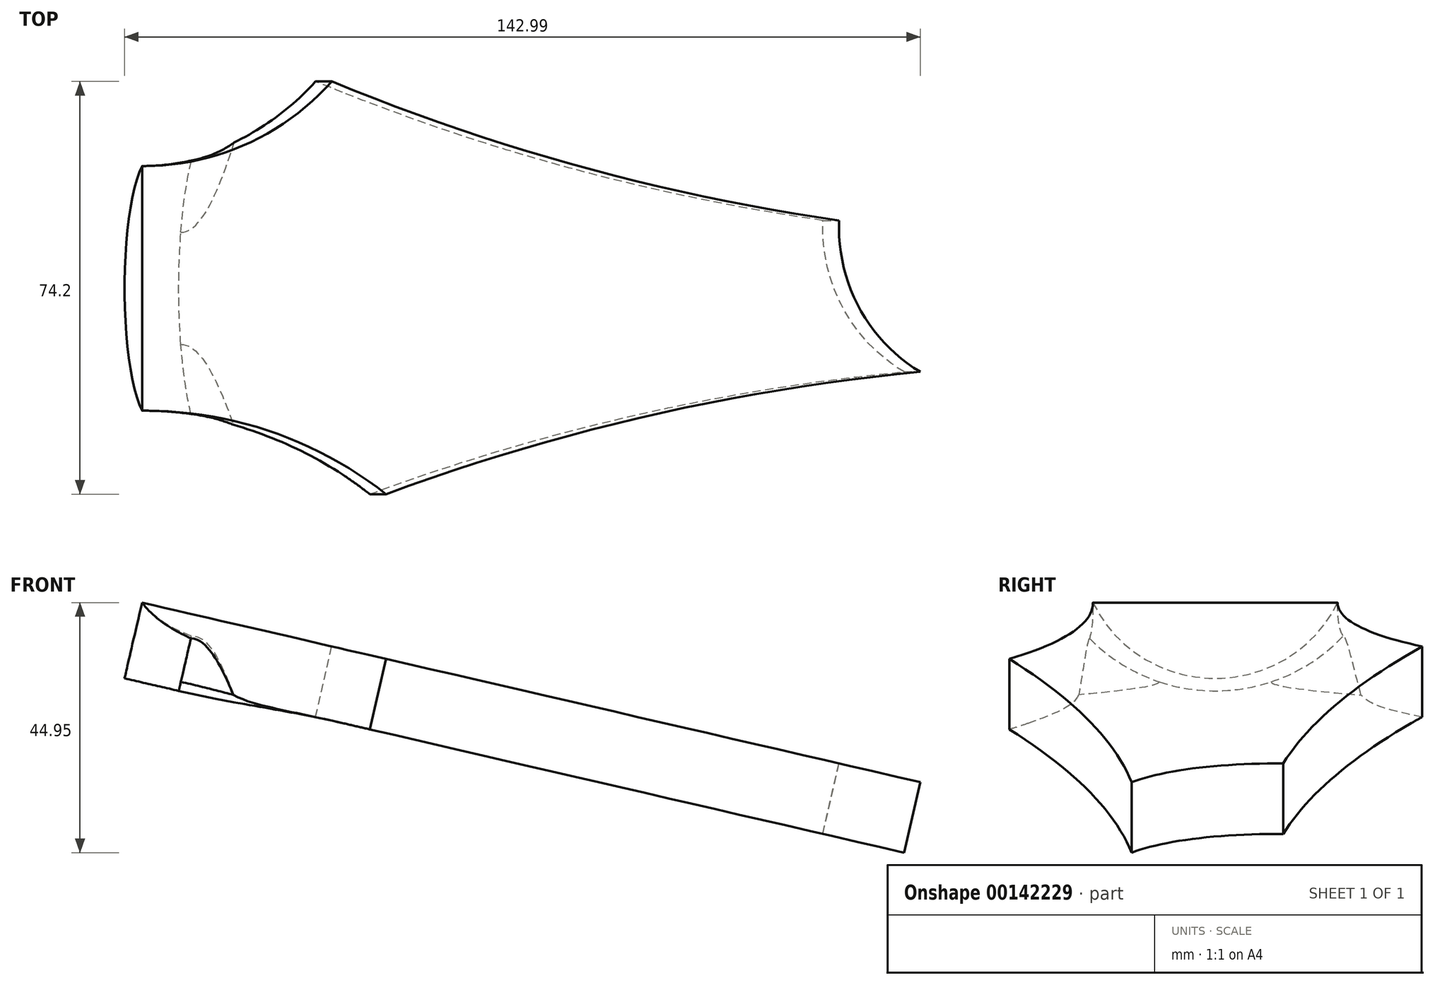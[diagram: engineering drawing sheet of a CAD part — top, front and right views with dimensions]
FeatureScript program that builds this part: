
annotation { "Feature Type Name" : "Feature", "Feature Type Description" : "" }
export const myFeature = defineFeature(function(context is Context, id is Id, definition is map)
    precondition{}
    {
        {
            var Q0;
            Q0=qCreatedBy(makeId("Top.planeOp"),FACE);
            var sketch = newSketch(context, id + "F0", { "sketchPlane" : qUnion([Q0])});
            skLineSegment(sketch, "E0", {"start": v(-562.39, 0) * mm, "end": v(989.83, 0) * mm, "construction": true});
            skLineSegment(sketch, "E1", {"start": v(685.7, 296.13) * mm, "end": v(685.7, -309.82) * mm, "construction": true});
            skLineSegment(sketch, "E2", {"start": v(0, 282.3) * mm, "end": v(0, -300.13) * mm, "construction": true});
            skPoint(sketch, "E3", {"position": v(0, 28.41) * mm});
            skPoint(sketch, "E4.MirrorP", {"position": v(0, -28.41) * mm});
            skPoint(sketch, "E5", {"position": v(685.7, 22) * mm});
            skPoint(sketch, "E6.MirrorP", {"position": v(685.7, -22) * mm});
            skLineSegment(sketch, "E7", {"start": v(0, 28.41) * mm, "end": v(685.7, 22) * mm, "construction": true});
            skLineSegment(sketch, "E8.MirrorCS", {"start": v(0, -28.41) * mm, "end": v(685.7, -22) * mm, "construction": true});
            skLineSegment(sketch, "E9", {"start": v(165.7, 98.55) * mm, "end": v(165.7, -119.87) * mm, "construction": true});
            skLineSegment(sketch, "E10", {"start": v(685.7, -22) * mm, "end": v(165.7, -26.86) * mm});
            skLineSegment(sketch, "E11", {"start": v(165.7, -26.86) * mm, "end": v(165.7, 26.86) * mm});
            skLineSegment(sketch, "E12", {"start": v(165.7, 26.86) * mm, "end": v(685.7, 22) * mm});
            skLineSegment(sketch, "E13", {"start": v(685.7, 22) * mm, "end": v(685.7, -22) * mm});
            skPoint(sketch, "E14.visualSharp", {"position": v(165.7, 26.86) * mm});
            skLineSegment(sketch, "E14.filletArc", {"start": v(165.7, 26.86) * mm, "end": v(165.7, 26.86) * mm});
            skPoint(sketch, "E15.visualSharp", {"position": v(165.7, -26.86) * mm});
            skLineSegment(sketch, "E15.filletArc", {"start": v(165.7, -26.86) * mm, "end": v(165.7, -26.86) * mm});
            skSolve(sketch);
        }
        {
            var Q0;
            Q0 = qSketchRegion(id + "F0", true);
            extrude(context, id + "F1", {"entities" : qUnion([Q0]), "depth" : 6 * mm});
        }
        {
            var Q0;
            Q0=makeQuery(id+"F1.opExtrude","SWEPT_FACE",FACE,{"disambiguationData":[OSD([sQuery(id+"F0.wireOp",EDGE,"E11")])]});
            var sketch = newSketch(context, id + "F2", { "sketchPlane" : qUnion([Q0])});
            skPoint(sketch, "E16", {"position": v(0, 6) * mm});
            skCircle(sketch, "E17", {"center": v(0, -400.4) * mm, "radius": 406.4 * mm});
            skSolve(sketch);
        }
        {
            var Q0;
            Q0 = qSketchRegion(id + "F2", true);
            extrude(context, id + "F3", {"entities" : qUnion([Q0]), "oppositeDirection" : true, "depth" : 520 * mm});
        }
        {
            var Q0;
            Q0=makeQuery(id+"F1.opExtrude","SWEPT_BODY",BODY,{"disambiguationData":[OSD([sQuery(id+"F0.wireOp",EDGE,"E10"),sQuery(id+"F0.wireOp",EDGE,"E11"),sQuery(id+"F0.wireOp",EDGE,"E12"),sQuery(id+"F0.wireOp",EDGE,"E13")])]});
            var Q1;
            Q1=makeQuery(id+"F3.opExtrude","SWEPT_BODY",BODY,{"disambiguationData":[OSD([sQuery(id+"F2.wireOp",EDGE,"E17")])]});
            booleanBodies(context, id + "F4", {"operationType" : BooleanOperationType.INTERSECTION, "tools" : qUnion([Q0, Q1])});
        }
        {
            var Q0;
            Q0=qCreatedBy(makeId("Top.planeOp"),FACE);
            var sketch = newSketch(context, id + "F5", { "sketchPlane" : qUnion([Q0])});
            skLineSegment(sketch, "E18.0", {"start": v(685.7, 296.13) * mm, "end": v(685.7, -309.82) * mm, "construction": true});
            skLineSegment(sketch, "E18.1", {"start": v(165.7, 98.55) * mm, "end": v(165.7, -119.87) * mm, "construction": true});
            skLineSegment(sketch, "E19.0", {"start": v(685.7, -22) * mm, "end": v(165.7, -26.86) * mm, "construction": true});
            skLineSegment(sketch, "E19.2", {"start": v(165.7, 26.86) * mm, "end": v(685.7, 22) * mm, "construction": true});
            skPoint(sketch, "E20", {"position": v(204.04, 0) * mm});
            skPoint(sketch, "E21", {"position": v(647.25, 0) * mm});
            skPoint(sketch, "E22", {"position": v(610.95, 0) * mm});
            skPoint(sketch, "E23", {"position": v(576.7, 0) * mm});
            skPoint(sketch, "E24", {"position": v(544.35, 0) * mm});
            skPoint(sketch, "E25", {"position": v(513.82, 0) * mm});
            skPoint(sketch, "E26", {"position": v(485, 0) * mm});
            skPoint(sketch, "E27", {"position": v(457.8, 0) * mm});
            skPoint(sketch, "E28", {"position": v(432.13, 0) * mm});
            skPoint(sketch, "E29", {"position": v(407.9, 0) * mm});
            skPoint(sketch, "E30", {"position": v(385.02, 0) * mm});
            skPoint(sketch, "E31", {"position": v(363.43, 0) * mm});
            skPoint(sketch, "E32", {"position": v(343.05, 0) * mm});
            skPoint(sketch, "E33", {"position": v(323.8, 0) * mm});
            skPoint(sketch, "E34", {"position": v(305.64, 0) * mm});
            skPoint(sketch, "E35", {"position": v(288.5, 0) * mm});
            skPoint(sketch, "E36", {"position": v(272.32, 0) * mm});
            skPoint(sketch, "E37", {"position": v(257.05, 0) * mm});
            skPoint(sketch, "E38", {"position": v(242.63, 0) * mm});
            skPoint(sketch, "E39", {"position": v(229.02, 0) * mm});
            skPoint(sketch, "E40", {"position": v(216.17, 0) * mm});
            skPoint(sketch, "E41", {"position": v(192.6, 0) * mm});
            skPoint(sketch, "E42", {"position": v(181.8, 0) * mm});
            skPoint(sketch, "E43", {"position": v(171.6, 0) * mm});
            skLineSegment(sketch, "E44", {"start": v(648.39, 22.35) * mm, "end": v(648.39, -22.35) * mm});
            skLineSegment(sketch, "E45", {"start": v(646.1, 22.37) * mm, "end": v(646.1, -22.37) * mm});
            skLineSegment(sketch, "E46", {"start": v(646.1, 22.37) * mm, "end": v(648.39, 22.35) * mm});
            skLineSegment(sketch, "E47", {"start": v(646.1, -22.37) * mm, "end": v(648.39, -22.35) * mm});
            skLineSegment(sketch, "E48", {"start": v(612.1, -22.69) * mm, "end": v(612.1, 22.69) * mm});
            skLineSegment(sketch, "E49", {"start": v(609.81, -22.7) * mm, "end": v(609.81, 22.7) * mm});
            skLineSegment(sketch, "E50", {"start": v(577.83, -23) * mm, "end": v(577.83, 23) * mm});
            skLineSegment(sketch, "E51", {"start": v(575.55, -23.03) * mm, "end": v(575.55, 23.03) * mm});
            skLineSegment(sketch, "E52", {"start": v(545.49, -23.31) * mm, "end": v(545.49, 23.31) * mm});
            skLineSegment(sketch, "E53", {"start": v(609.81, -22.7) * mm, "end": v(612.1, -22.69) * mm});
            skLineSegment(sketch, "E54", {"start": v(609.81, 22.7) * mm, "end": v(612.1, 22.69) * mm});
            skLineSegment(sketch, "E55", {"start": v(575.55, 23.03) * mm, "end": v(577.83, 23) * mm});
            skLineSegment(sketch, "E56", {"start": v(575.55, -23.03) * mm, "end": v(577.83, -23) * mm});
            skLineSegment(sketch, "E57", {"start": v(543.2, 23.33) * mm, "end": v(543.2, -23.33) * mm});
            skLineSegment(sketch, "E58", {"start": v(514.96, 23.6) * mm, "end": v(514.96, -23.6) * mm});
            skLineSegment(sketch, "E59", {"start": v(512.68, 23.62) * mm, "end": v(512.68, -23.62) * mm});
            skLineSegment(sketch, "E60", {"start": v(486.15, 23.87) * mm, "end": v(486.15, -23.87) * mm});
            skLineSegment(sketch, "E61", {"start": v(483.87, 23.89) * mm, "end": v(483.87, -23.89) * mm});
            skLineSegment(sketch, "E62", {"start": v(458.95, 24.12) * mm, "end": v(458.95, -24.12) * mm});
            skLineSegment(sketch, "E63", {"start": v(456.67, 24.14) * mm, "end": v(456.67, -24.14) * mm});
            skLineSegment(sketch, "E64", {"start": v(433.27, -24.36) * mm, "end": v(433.27, 24.36) * mm});
            skLineSegment(sketch, "E65", {"start": v(431, -24.38) * mm, "end": v(431, 24.38) * mm});
            skLineSegment(sketch, "E66", {"start": v(409.04, -24.59) * mm, "end": v(409.04, 24.59) * mm});
            skLineSegment(sketch, "E67", {"start": v(406.76, -24.6) * mm, "end": v(406.76, 24.6) * mm});
            skLineSegment(sketch, "E68", {"start": v(543.2, -23.33) * mm, "end": v(545.49, -23.31) * mm});
            skLineSegment(sketch, "E69", {"start": v(512.68, -23.62) * mm, "end": v(514.96, -23.6) * mm});
            skLineSegment(sketch, "E70", {"start": v(483.87, -23.89) * mm, "end": v(486.15, -23.87) * mm});
            skLineSegment(sketch, "E71", {"start": v(456.67, -24.14) * mm, "end": v(458.95, -24.12) * mm});
            skLineSegment(sketch, "E72", {"start": v(431, -24.38) * mm, "end": v(433.27, -24.36) * mm});
            skLineSegment(sketch, "E73", {"start": v(431, 24.38) * mm, "end": v(433.27, 24.36) * mm});
            skLineSegment(sketch, "E74", {"start": v(456.67, 24.14) * mm, "end": v(458.95, 24.12) * mm});
            skLineSegment(sketch, "E75", {"start": v(483.87, 23.89) * mm, "end": v(486.15, 23.87) * mm});
            skLineSegment(sketch, "E76", {"start": v(512.68, 23.62) * mm, "end": v(514.96, 23.6) * mm});
            skLineSegment(sketch, "E77", {"start": v(543.2, 23.33) * mm, "end": v(545.49, 23.31) * mm});
            skLineSegment(sketch, "E78", {"start": v(386.16, 24.8) * mm, "end": v(386.16, -24.8) * mm});
            skLineSegment(sketch, "E79", {"start": v(383.88, 24.82) * mm, "end": v(383.88, -24.82) * mm});
            skLineSegment(sketch, "E80", {"start": v(364.57, 25) * mm, "end": v(364.57, -25) * mm});
            skLineSegment(sketch, "E81", {"start": v(362.52, 25.02) * mm, "end": v(362.05, -25.03) * mm});
            skLineSegment(sketch, "E82", {"start": v(409.04, -24.59) * mm, "end": v(406.76, -24.6) * mm});
            skLineSegment(sketch, "E83", {"start": v(406.76, 24.6) * mm, "end": v(409.04, 24.59) * mm});
            skLineSegment(sketch, "E84", {"start": v(383.88, 24.82) * mm, "end": v(386.16, 24.8) * mm});
            skLineSegment(sketch, "E85", {"start": v(383.88, -24.82) * mm, "end": v(386.16, -24.8) * mm});
            skLineSegment(sketch, "E86", {"start": v(364.57, -25) * mm, "end": v(362.05, -25.03) * mm});
            skLineSegment(sketch, "E87", {"start": v(362.52, 25.02) * mm, "end": v(364.57, 25) * mm});
            skLineSegment(sketch, "E88", {"start": v(344.19, 25.2) * mm, "end": v(344.19, -25.2) * mm});
            skLineSegment(sketch, "E89", {"start": v(341.9, -25.22) * mm, "end": v(341.9, 25.22) * mm});
            skLineSegment(sketch, "E90", {"start": v(324.95, -25.38) * mm, "end": v(324.95, 25.38) * mm});
            skLineSegment(sketch, "E91", {"start": v(322.67, -25.4) * mm, "end": v(322.67, 25.4) * mm});
            skLineSegment(sketch, "E92", {"start": v(306.78, -25.54) * mm, "end": v(306.78, 25.54) * mm});
            skLineSegment(sketch, "E93", {"start": v(304.5, -25.57) * mm, "end": v(304.5, 25.57) * mm});
            skLineSegment(sketch, "E94", {"start": v(289.64, -25.7) * mm, "end": v(289.64, 25.7) * mm});
            skLineSegment(sketch, "E95", {"start": v(287.36, -25.73) * mm, "end": v(287.36, 25.73) * mm});
            skLineSegment(sketch, "E96", {"start": v(273.46, -25.86) * mm, "end": v(273.46, 25.86) * mm});
            skLineSegment(sketch, "E97", {"start": v(271.18, -25.88) * mm, "end": v(271.18, 25.88) * mm});
            skLineSegment(sketch, "E98", {"start": v(344.19, -25.2) * mm, "end": v(341.9, -25.22) * mm});
            skLineSegment(sketch, "E99", {"start": v(324.95, -25.38) * mm, "end": v(322.67, -25.4) * mm});
            skLineSegment(sketch, "E100", {"start": v(289.64, -25.7) * mm, "end": v(287.36, -25.73) * mm});
            skLineSegment(sketch, "E101", {"start": v(273.46, -25.86) * mm, "end": v(271.18, -25.88) * mm});
            skLineSegment(sketch, "E102", {"start": v(271.18, 25.88) * mm, "end": v(273.46, 25.86) * mm});
            skLineSegment(sketch, "E103", {"start": v(287.36, 25.73) * mm, "end": v(289.64, 25.7) * mm});
            skLineSegment(sketch, "E104", {"start": v(304.5, 25.57) * mm, "end": v(306.78, 25.54) * mm});
            skLineSegment(sketch, "E105", {"start": v(322.67, 25.4) * mm, "end": v(324.95, 25.38) * mm});
            skLineSegment(sketch, "E106", {"start": v(304.5, -25.57) * mm, "end": v(306.78, -25.54) * mm});
            skLineSegment(sketch, "E107", {"start": v(341.9, 25.22) * mm, "end": v(344.19, 25.2) * mm});
            skLineSegment(sketch, "E108", {"start": v(258.19, -26) * mm, "end": v(258.19, 26) * mm});
            skLineSegment(sketch, "E109", {"start": v(243.77, -26.13) * mm, "end": v(243.77, 26.13) * mm});
            skLineSegment(sketch, "E110", {"start": v(230.16, -26.26) * mm, "end": v(230.16, 26.26) * mm});
            skLineSegment(sketch, "E111", {"start": v(217.31, -26.38) * mm, "end": v(217.31, 26.38) * mm});
            skLineSegment(sketch, "E112", {"start": v(205.18, -26.5) * mm, "end": v(205.18, 26.5) * mm});
            skLineSegment(sketch, "E113", {"start": v(193.74, -26.6) * mm, "end": v(193.74, 26.6) * mm});
            skLineSegment(sketch, "E114", {"start": v(182.93, -26.7) * mm, "end": v(182.93, 26.7) * mm});
            skLineSegment(sketch, "E115", {"start": v(172.74, -26.8) * mm, "end": v(172.74, 26.8) * mm});
            skLineSegment(sketch, "E116", {"start": v(170.46, -26.82) * mm, "end": v(170.46, 26.8) * mm});
            skLineSegment(sketch, "E117", {"start": v(180.65, -26.72) * mm, "end": v(180.65, 26.72) * mm});
            skLineSegment(sketch, "E118", {"start": v(191.46, -26.62) * mm, "end": v(191.46, 26.62) * mm});
            skLineSegment(sketch, "E119", {"start": v(202.9, -26.52) * mm, "end": v(202.9, 26.52) * mm});
            skLineSegment(sketch, "E120", {"start": v(215.03, -26.4) * mm, "end": v(215.03, 26.4) * mm});
            skLineSegment(sketch, "E121", {"start": v(227.88, -26.28) * mm, "end": v(227.88, 26.28) * mm});
            skLineSegment(sketch, "E122", {"start": v(241.49, -26.16) * mm, "end": v(241.49, 26.16) * mm});
            skLineSegment(sketch, "E123", {"start": v(255.9, -26.02) * mm, "end": v(255.9, 26.02) * mm});
            skLineSegment(sketch, "E124", {"start": v(258.19, -26) * mm, "end": v(255.9, -26.02) * mm});
            skLineSegment(sketch, "E125", {"start": v(243.77, -26.13) * mm, "end": v(241.49, -26.16) * mm});
            skLineSegment(sketch, "E126", {"start": v(230.16, -26.26) * mm, "end": v(227.88, -26.28) * mm});
            skLineSegment(sketch, "E127", {"start": v(217.31, -26.38) * mm, "end": v(215.03, -26.4) * mm});
            skLineSegment(sketch, "E128", {"start": v(205.18, -26.5) * mm, "end": v(202.9, -26.52) * mm});
            skLineSegment(sketch, "E129", {"start": v(193.74, -26.6) * mm, "end": v(191.46, -26.62) * mm});
            skLineSegment(sketch, "E130", {"start": v(182.93, -26.7) * mm, "end": v(180.65, -26.72) * mm});
            skLineSegment(sketch, "E131", {"start": v(172.74, -26.8) * mm, "end": v(170.46, -26.82) * mm});
            skLineSegment(sketch, "E132", {"start": v(170.46, 26.8) * mm, "end": v(172.74, 26.8) * mm});
            skLineSegment(sketch, "E133", {"start": v(180.65, 26.72) * mm, "end": v(182.93, 26.7) * mm});
            skLineSegment(sketch, "E134", {"start": v(191.46, 26.62) * mm, "end": v(193.74, 26.6) * mm});
            skLineSegment(sketch, "E135", {"start": v(202.9, 26.52) * mm, "end": v(205.18, 26.5) * mm});
            skLineSegment(sketch, "E136", {"start": v(215.03, 26.4) * mm, "end": v(217.31, 26.38) * mm});
            skLineSegment(sketch, "E137", {"start": v(227.88, 26.28) * mm, "end": v(230.16, 26.26) * mm});
            skLineSegment(sketch, "E138", {"start": v(241.49, 26.16) * mm, "end": v(243.77, 26.13) * mm});
            skLineSegment(sketch, "E139", {"start": v(255.9, 26.02) * mm, "end": v(258.19, 26) * mm});
            skSolve(sketch);
        }
        {
            var Q0;
            Q0 = qSketchRegion(id + "F5", true);
            extrude(context, id + "F6", {"entities" : qUnion([Q0]), "operationType" : NewBodyOperationType.ADD, "depth" : 7.4 * mm});
        }
        {
            var Q0;
            Q0=makeQuery(id+"F1.opExtrude","SWEPT_FACE",FACE,{"disambiguationData":[OSD([sQuery(id+"F0.wireOp",EDGE,"E11")])]});
            var sketch = newSketch(context, id + "F7", { "sketchPlane" : qUnion([Q0])});
            skCircle(sketch, "E140.0", {"center": v(0, -400.4) * mm, "radius": 406.4 * mm, "construction": true});
            skCircle(sketch, "E141", {"center": v(0, -399) * mm, "radius": 406.4 * mm});
            skSolve(sketch);
        }
        {
            var Q0;
            Q0 = qSketchRegion(id + "F7", true);
            extrude(context, id + "F8", {"entities" : qUnion([Q0]), "oppositeDirection" : true, "depth" : 520 * mm});
        }
        {
            var Q0;
            Q0=makeQuery(id+"F4.opBoolean","INTERSECT",BODY,{"derivedFrom":[makeQuery(id+"F1.opExtrude","SWEPT_BODY",BODY,{"disambiguationData":[OSD([sQuery(id+"F0.wireOp",EDGE,"E10"),sQuery(id+"F0.wireOp",EDGE,"E11"),sQuery(id+"F0.wireOp",EDGE,"E12"),sQuery(id+"F0.wireOp",EDGE,"E13")])]}),makeQuery(id+"F3.opExtrude","SWEPT_BODY",BODY,{"disambiguationData":[OSD([sQuery(id+"F2.wireOp",EDGE,"E17")])]})]});
            var Q1;
            Q1=makeQuery(id+"F8.opExtrude","SWEPT_BODY",BODY,{"disambiguationData":[OSD([sQuery(id+"F7.wireOp",EDGE,"E141")])]});
            booleanBodies(context, id + "F9", {"operationType" : BooleanOperationType.INTERSECTION, "tools" : qUnion([Q0, Q1])});
        }
        {
            var Q0;
            Q0=makeQuery(id+"F9.opBoolean","INTERSECT",EDGE,{"derivedFrom":[makeQuery(id+"F6.opExtrude","SWEPT_FACE",FACE,{"disambiguationData":[OSD([sQuery(id+"F5.wireOp",EDGE,"E116")])]}),makeQuery(id+"F8.opExtrude","SWEPT_FACE",FACE,{"disambiguationData":[OSD([sQuery(id+"F7.wireOp",EDGE,"E141")])]})]});
            var Q1;
            Q1=makeQuery(id+"F9.opBoolean","INTERSECT",EDGE,{"derivedFrom":[makeQuery(id+"F6.opExtrude","SWEPT_FACE",FACE,{"disambiguationData":[OSD([sQuery(id+"F5.wireOp",EDGE,"E115")])]}),makeQuery(id+"F8.opExtrude","SWEPT_FACE",FACE,{"disambiguationData":[OSD([sQuery(id+"F7.wireOp",EDGE,"E141")])]})]});
            var Q2;
            Q2=makeQuery(id+"F9.opBoolean","INTERSECT",EDGE,{"derivedFrom":[makeQuery(id+"F6.opExtrude","SWEPT_FACE",FACE,{"disambiguationData":[OSD([sQuery(id+"F5.wireOp",EDGE,"E117")])]}),makeQuery(id+"F8.opExtrude","SWEPT_FACE",FACE,{"disambiguationData":[OSD([sQuery(id+"F7.wireOp",EDGE,"E141")])]})]});
            var Q3;
            Q3=makeQuery(id+"F9.opBoolean","INTERSECT",EDGE,{"derivedFrom":[makeQuery(id+"F6.opExtrude","SWEPT_FACE",FACE,{"disambiguationData":[OSD([sQuery(id+"F5.wireOp",EDGE,"E114")])]}),makeQuery(id+"F8.opExtrude","SWEPT_FACE",FACE,{"disambiguationData":[OSD([sQuery(id+"F7.wireOp",EDGE,"E141")])]})]});
            var Q4;
            Q4=makeQuery(id+"F9.opBoolean","INTERSECT",EDGE,{"derivedFrom":[makeQuery(id+"F6.opExtrude","SWEPT_FACE",FACE,{"disambiguationData":[OSD([sQuery(id+"F5.wireOp",EDGE,"E118")])]}),makeQuery(id+"F8.opExtrude","SWEPT_FACE",FACE,{"disambiguationData":[OSD([sQuery(id+"F7.wireOp",EDGE,"E141")])]})]});
            var Q5;
            Q5=makeQuery(id+"F9.opBoolean","INTERSECT",EDGE,{"derivedFrom":[makeQuery(id+"F6.opExtrude","SWEPT_FACE",FACE,{"disambiguationData":[OSD([sQuery(id+"F5.wireOp",EDGE,"E113")])]}),makeQuery(id+"F8.opExtrude","SWEPT_FACE",FACE,{"disambiguationData":[OSD([sQuery(id+"F7.wireOp",EDGE,"E141")])]})]});
            var Q6;
            Q6=makeQuery(id+"F9.opBoolean","INTERSECT",EDGE,{"derivedFrom":[makeQuery(id+"F6.opExtrude","SWEPT_FACE",FACE,{"disambiguationData":[OSD([sQuery(id+"F5.wireOp",EDGE,"E119")])]}),makeQuery(id+"F8.opExtrude","SWEPT_FACE",FACE,{"disambiguationData":[OSD([sQuery(id+"F7.wireOp",EDGE,"E141")])]})]});
            var Q7;
            Q7=makeQuery(id+"F9.opBoolean","INTERSECT",EDGE,{"derivedFrom":[makeQuery(id+"F6.opExtrude","SWEPT_FACE",FACE,{"disambiguationData":[OSD([sQuery(id+"F5.wireOp",EDGE,"E112")])]}),makeQuery(id+"F8.opExtrude","SWEPT_FACE",FACE,{"disambiguationData":[OSD([sQuery(id+"F7.wireOp",EDGE,"E141")])]})]});
            var Q8;
            Q8=makeQuery(id+"F9.opBoolean","INTERSECT",EDGE,{"derivedFrom":[makeQuery(id+"F6.opExtrude","SWEPT_FACE",FACE,{"disambiguationData":[OSD([sQuery(id+"F5.wireOp",EDGE,"E120")])]}),makeQuery(id+"F8.opExtrude","SWEPT_FACE",FACE,{"disambiguationData":[OSD([sQuery(id+"F7.wireOp",EDGE,"E141")])]})]});
            var Q9;
            Q9=makeQuery(id+"F9.opBoolean","INTERSECT",EDGE,{"derivedFrom":[makeQuery(id+"F6.opExtrude","SWEPT_FACE",FACE,{"disambiguationData":[OSD([sQuery(id+"F5.wireOp",EDGE,"E111")])]}),makeQuery(id+"F8.opExtrude","SWEPT_FACE",FACE,{"disambiguationData":[OSD([sQuery(id+"F7.wireOp",EDGE,"E141")])]})]});
            var Q10;
            Q10=makeQuery(id+"F9.opBoolean","INTERSECT",EDGE,{"derivedFrom":[makeQuery(id+"F6.opExtrude","SWEPT_FACE",FACE,{"disambiguationData":[OSD([sQuery(id+"F5.wireOp",EDGE,"E121")])]}),makeQuery(id+"F8.opExtrude","SWEPT_FACE",FACE,{"disambiguationData":[OSD([sQuery(id+"F7.wireOp",EDGE,"E141")])]})]});
            var Q11;
            Q11=makeQuery(id+"F9.opBoolean","INTERSECT",EDGE,{"derivedFrom":[makeQuery(id+"F6.opExtrude","SWEPT_FACE",FACE,{"disambiguationData":[OSD([sQuery(id+"F5.wireOp",EDGE,"E110")])]}),makeQuery(id+"F8.opExtrude","SWEPT_FACE",FACE,{"disambiguationData":[OSD([sQuery(id+"F7.wireOp",EDGE,"E141")])]})]});
            var Q12;
            Q12=makeQuery(id+"F9.opBoolean","INTERSECT",EDGE,{"derivedFrom":[makeQuery(id+"F6.opExtrude","SWEPT_FACE",FACE,{"disambiguationData":[OSD([sQuery(id+"F5.wireOp",EDGE,"E122")])]}),makeQuery(id+"F8.opExtrude","SWEPT_FACE",FACE,{"disambiguationData":[OSD([sQuery(id+"F7.wireOp",EDGE,"E141")])]})]});
            var Q13;
            Q13=makeQuery(id+"F9.opBoolean","INTERSECT",EDGE,{"derivedFrom":[makeQuery(id+"F6.opExtrude","SWEPT_FACE",FACE,{"disambiguationData":[OSD([sQuery(id+"F5.wireOp",EDGE,"E109")])]}),makeQuery(id+"F8.opExtrude","SWEPT_FACE",FACE,{"disambiguationData":[OSD([sQuery(id+"F7.wireOp",EDGE,"E141")])]})]});
            var Q14;
            Q14=makeQuery(id+"F9.opBoolean","INTERSECT",EDGE,{"derivedFrom":[makeQuery(id+"F6.opExtrude","SWEPT_FACE",FACE,{"disambiguationData":[OSD([sQuery(id+"F5.wireOp",EDGE,"E123")])]}),makeQuery(id+"F8.opExtrude","SWEPT_FACE",FACE,{"disambiguationData":[OSD([sQuery(id+"F7.wireOp",EDGE,"E141")])]})]});
            var Q15;
            Q15=makeQuery(id+"F9.opBoolean","INTERSECT",EDGE,{"derivedFrom":[makeQuery(id+"F6.opExtrude","SWEPT_FACE",FACE,{"disambiguationData":[OSD([sQuery(id+"F5.wireOp",EDGE,"E108")])]}),makeQuery(id+"F8.opExtrude","SWEPT_FACE",FACE,{"disambiguationData":[OSD([sQuery(id+"F7.wireOp",EDGE,"E141")])]})]});
            var Q16;
            Q16=makeQuery(id+"F9.opBoolean","INTERSECT",EDGE,{"derivedFrom":[makeQuery(id+"F6.opExtrude","SWEPT_FACE",FACE,{"disambiguationData":[OSD([sQuery(id+"F5.wireOp",EDGE,"E97")])]}),makeQuery(id+"F8.opExtrude","SWEPT_FACE",FACE,{"disambiguationData":[OSD([sQuery(id+"F7.wireOp",EDGE,"E141")])]})]});
            var Q17;
            Q17=makeQuery(id+"F9.opBoolean","INTERSECT",EDGE,{"derivedFrom":[makeQuery(id+"F6.opExtrude","SWEPT_FACE",FACE,{"disambiguationData":[OSD([sQuery(id+"F5.wireOp",EDGE,"E96")])]}),makeQuery(id+"F8.opExtrude","SWEPT_FACE",FACE,{"disambiguationData":[OSD([sQuery(id+"F7.wireOp",EDGE,"E141")])]})]});
            var Q18;
            Q18=makeQuery(id+"F9.opBoolean","INTERSECT",EDGE,{"derivedFrom":[makeQuery(id+"F6.opExtrude","SWEPT_FACE",FACE,{"disambiguationData":[OSD([sQuery(id+"F5.wireOp",EDGE,"E95")])]}),makeQuery(id+"F8.opExtrude","SWEPT_FACE",FACE,{"disambiguationData":[OSD([sQuery(id+"F7.wireOp",EDGE,"E141")])]})]});
            var Q19;
            Q19=makeQuery(id+"F9.opBoolean","INTERSECT",EDGE,{"derivedFrom":[makeQuery(id+"F6.opExtrude","SWEPT_FACE",FACE,{"disambiguationData":[OSD([sQuery(id+"F5.wireOp",EDGE,"E94")])]}),makeQuery(id+"F8.opExtrude","SWEPT_FACE",FACE,{"disambiguationData":[OSD([sQuery(id+"F7.wireOp",EDGE,"E141")])]})]});
            var Q20;
            Q20=makeQuery(id+"F9.opBoolean","INTERSECT",EDGE,{"derivedFrom":[makeQuery(id+"F6.opExtrude","SWEPT_FACE",FACE,{"disambiguationData":[OSD([sQuery(id+"F5.wireOp",EDGE,"E93")])]}),makeQuery(id+"F8.opExtrude","SWEPT_FACE",FACE,{"disambiguationData":[OSD([sQuery(id+"F7.wireOp",EDGE,"E141")])]})]});
            var Q21;
            Q21=makeQuery(id+"F9.opBoolean","INTERSECT",EDGE,{"derivedFrom":[makeQuery(id+"F6.opExtrude","SWEPT_FACE",FACE,{"disambiguationData":[OSD([sQuery(id+"F5.wireOp",EDGE,"E92")])]}),makeQuery(id+"F8.opExtrude","SWEPT_FACE",FACE,{"disambiguationData":[OSD([sQuery(id+"F7.wireOp",EDGE,"E141")])]})]});
            var Q22;
            Q22=makeQuery(id+"F9.opBoolean","INTERSECT",EDGE,{"derivedFrom":[makeQuery(id+"F6.opExtrude","SWEPT_FACE",FACE,{"disambiguationData":[OSD([sQuery(id+"F5.wireOp",EDGE,"E91")])]}),makeQuery(id+"F8.opExtrude","SWEPT_FACE",FACE,{"disambiguationData":[OSD([sQuery(id+"F7.wireOp",EDGE,"E141")])]})]});
            var Q23;
            Q23=makeQuery(id+"F9.opBoolean","INTERSECT",EDGE,{"derivedFrom":[makeQuery(id+"F6.opExtrude","SWEPT_FACE",FACE,{"disambiguationData":[OSD([sQuery(id+"F5.wireOp",EDGE,"E90")])]}),makeQuery(id+"F8.opExtrude","SWEPT_FACE",FACE,{"disambiguationData":[OSD([sQuery(id+"F7.wireOp",EDGE,"E141")])]})]});
            var Q24;
            Q24=makeQuery(id+"F9.opBoolean","INTERSECT",EDGE,{"derivedFrom":[makeQuery(id+"F6.opExtrude","SWEPT_FACE",FACE,{"disambiguationData":[OSD([sQuery(id+"F5.wireOp",EDGE,"E89")])]}),makeQuery(id+"F8.opExtrude","SWEPT_FACE",FACE,{"disambiguationData":[OSD([sQuery(id+"F7.wireOp",EDGE,"E141")])]})]});
            var Q25;
            Q25=makeQuery(id+"F9.opBoolean","INTERSECT",EDGE,{"derivedFrom":[makeQuery(id+"F6.opExtrude","SWEPT_FACE",FACE,{"disambiguationData":[OSD([sQuery(id+"F5.wireOp",EDGE,"E88")])]}),makeQuery(id+"F8.opExtrude","SWEPT_FACE",FACE,{"disambiguationData":[OSD([sQuery(id+"F7.wireOp",EDGE,"E141")])]})]});
            var Q26;
            Q26=makeQuery(id+"F9.opBoolean","INTERSECT",EDGE,{"derivedFrom":[makeQuery(id+"F6.opExtrude","SWEPT_FACE",FACE,{"disambiguationData":[OSD([sQuery(id+"F5.wireOp",EDGE,"E81")])]}),makeQuery(id+"F8.opExtrude","SWEPT_FACE",FACE,{"disambiguationData":[OSD([sQuery(id+"F7.wireOp",EDGE,"E141")])]})]});
            var Q27;
            Q27=makeQuery(id+"F9.opBoolean","INTERSECT",EDGE,{"derivedFrom":[makeQuery(id+"F6.opExtrude","SWEPT_FACE",FACE,{"disambiguationData":[OSD([sQuery(id+"F5.wireOp",EDGE,"E80")])]}),makeQuery(id+"F8.opExtrude","SWEPT_FACE",FACE,{"disambiguationData":[OSD([sQuery(id+"F7.wireOp",EDGE,"E141")])]})]});
            var Q28;
            Q28=makeQuery(id+"F9.opBoolean","INTERSECT",EDGE,{"derivedFrom":[makeQuery(id+"F6.opExtrude","SWEPT_FACE",FACE,{"disambiguationData":[OSD([sQuery(id+"F5.wireOp",EDGE,"E79")])]}),makeQuery(id+"F8.opExtrude","SWEPT_FACE",FACE,{"disambiguationData":[OSD([sQuery(id+"F7.wireOp",EDGE,"E141")])]})]});
            var Q29;
            Q29=makeQuery(id+"F9.opBoolean","INTERSECT",EDGE,{"derivedFrom":[makeQuery(id+"F6.opExtrude","SWEPT_FACE",FACE,{"disambiguationData":[OSD([sQuery(id+"F5.wireOp",EDGE,"E78")])]}),makeQuery(id+"F8.opExtrude","SWEPT_FACE",FACE,{"disambiguationData":[OSD([sQuery(id+"F7.wireOp",EDGE,"E141")])]})]});
            var Q30;
            Q30=makeQuery(id+"F9.opBoolean","INTERSECT",EDGE,{"derivedFrom":[makeQuery(id+"F6.opExtrude","SWEPT_FACE",FACE,{"disambiguationData":[OSD([sQuery(id+"F5.wireOp",EDGE,"E67")])]}),makeQuery(id+"F8.opExtrude","SWEPT_FACE",FACE,{"disambiguationData":[OSD([sQuery(id+"F7.wireOp",EDGE,"E141")])]})]});
            var Q31;
            Q31=makeQuery(id+"F9.opBoolean","INTERSECT",EDGE,{"derivedFrom":[makeQuery(id+"F6.opExtrude","SWEPT_FACE",FACE,{"disambiguationData":[OSD([sQuery(id+"F5.wireOp",EDGE,"E66")])]}),makeQuery(id+"F8.opExtrude","SWEPT_FACE",FACE,{"disambiguationData":[OSD([sQuery(id+"F7.wireOp",EDGE,"E141")])]})]});
            var Q32;
            Q32=makeQuery(id+"F9.opBoolean","INTERSECT",EDGE,{"derivedFrom":[makeQuery(id+"F6.opExtrude","SWEPT_FACE",FACE,{"disambiguationData":[OSD([sQuery(id+"F5.wireOp",EDGE,"E67")])]}),makeQuery(id+"F8.opExtrude","SWEPT_FACE",FACE,{"disambiguationData":[OSD([sQuery(id+"F7.wireOp",EDGE,"E141")])]})]});
            var Q33;
            Q33=makeQuery(id+"F9.opBoolean","INTERSECT",EDGE,{"disambiguationData":[OD(7.0)],"derivedFrom":[makeQuery(id+"F6.boolean.opBoolean","MERGE",FACE,{"derivedFrom":[makeQuery(id+"F1.opExtrude","SWEPT_FACE",FACE,{"disambiguationData":[OSD([sQuery(id+"F0.wireOp",EDGE,"E10")])]}),makeQuery(id+"F6.opExtrude","SWEPT_FACE",FACE,{"disambiguationData":[OSD([sQuery(id+"F5.wireOp",EDGE,"E47")])]}),makeQuery(id+"F6.opExtrude","SWEPT_FACE",FACE,{"disambiguationData":[OSD([sQuery(id+"F5.wireOp",EDGE,"E53")])]}),makeQuery(id+"F6.opExtrude","SWEPT_FACE",FACE,{"disambiguationData":[OSD([sQuery(id+"F5.wireOp",EDGE,"E56")])]}),makeQuery(id+"F6.opExtrude","SWEPT_FACE",FACE,{"disambiguationData":[OSD([sQuery(id+"F5.wireOp",EDGE,"E68")])]}),makeQuery(id+"F6.opExtrude","SWEPT_FACE",FACE,{"disambiguationData":[OSD([sQuery(id+"F5.wireOp",EDGE,"E69")])]}),makeQuery(id+"F6.opExtrude","SWEPT_FACE",FACE,{"disambiguationData":[OSD([sQuery(id+"F5.wireOp",EDGE,"E70")])]}),makeQuery(id+"F6.opExtrude","SWEPT_FACE",FACE,{"disambiguationData":[OSD([sQuery(id+"F5.wireOp",EDGE,"E71")])]}),makeQuery(id+"F6.opExtrude","SWEPT_FACE",FACE,{"disambiguationData":[OSD([sQuery(id+"F5.wireOp",EDGE,"E72")])]}),makeQuery(id+"F6.opExtrude","SWEPT_FACE",FACE,{"disambiguationData":[OSD([sQuery(id+"F5.wireOp",EDGE,"E82")])]}),makeQuery(id+"F6.opExtrude","SWEPT_FACE",FACE,{"disambiguationData":[OSD([sQuery(id+"F5.wireOp",EDGE,"E85")])]}),makeQuery(id+"F6.opExtrude","SWEPT_FACE",FACE,{"disambiguationData":[OSD([sQuery(id+"F5.wireOp",EDGE,"E86")])]}),makeQuery(id+"F6.opExtrude","SWEPT_FACE",FACE,{"disambiguationData":[OSD([sQuery(id+"F5.wireOp",EDGE,"E98")])]}),makeQuery(id+"F6.opExtrude","SWEPT_FACE",FACE,{"disambiguationData":[OSD([sQuery(id+"F5.wireOp",EDGE,"E99")])]}),makeQuery(id+"F6.opExtrude","SWEPT_FACE",FACE,{"disambiguationData":[OSD([sQuery(id+"F5.wireOp",EDGE,"E100")])]}),makeQuery(id+"F6.opExtrude","SWEPT_FACE",FACE,{"disambiguationData":[OSD([sQuery(id+"F5.wireOp",EDGE,"E101")])]}),makeQuery(id+"F6.opExtrude","SWEPT_FACE",FACE,{"disambiguationData":[OSD([sQuery(id+"F5.wireOp",EDGE,"E106")])]}),makeQuery(id+"F6.opExtrude","SWEPT_FACE",FACE,{"disambiguationData":[OSD([sQuery(id+"F5.wireOp",EDGE,"E124")])]}),makeQuery(id+"F6.opExtrude","SWEPT_FACE",FACE,{"disambiguationData":[OSD([sQuery(id+"F5.wireOp",EDGE,"E125")])]}),makeQuery(id+"F6.opExtrude","SWEPT_FACE",FACE,{"disambiguationData":[OSD([sQuery(id+"F5.wireOp",EDGE,"E126")])]}),makeQuery(id+"F6.opExtrude","SWEPT_FACE",FACE,{"disambiguationData":[OSD([sQuery(id+"F5.wireOp",EDGE,"E127")])]}),makeQuery(id+"F6.opExtrude","SWEPT_FACE",FACE,{"disambiguationData":[OSD([sQuery(id+"F5.wireOp",EDGE,"E128")])]}),makeQuery(id+"F6.opExtrude","SWEPT_FACE",FACE,{"disambiguationData":[OSD([sQuery(id+"F5.wireOp",EDGE,"E129")])]}),makeQuery(id+"F6.opExtrude","SWEPT_FACE",FACE,{"disambiguationData":[OSD([sQuery(id+"F5.wireOp",EDGE,"E130")])]}),makeQuery(id+"F6.opExtrude","SWEPT_FACE",FACE,{"disambiguationData":[OSD([sQuery(id+"F5.wireOp",EDGE,"E131")])]})]}),makeQuery(id+"F8.opExtrude","SWEPT_FACE",FACE,{"disambiguationData":[OSD([sQuery(id+"F7.wireOp",EDGE,"E141")])]})]});
            var Q34;
            Q34=makeQuery(id+"F9.opBoolean","INTERSECT",EDGE,{"derivedFrom":[makeQuery(id+"F6.opExtrude","SWEPT_FACE",FACE,{"disambiguationData":[OSD([sQuery(id+"F5.wireOp",EDGE,"E65")])]}),makeQuery(id+"F8.opExtrude","SWEPT_FACE",FACE,{"disambiguationData":[OSD([sQuery(id+"F7.wireOp",EDGE,"E141")])]})]});
            var Q35;
            Q35=makeQuery(id+"F9.opBoolean","INTERSECT",EDGE,{"derivedFrom":[makeQuery(id+"F6.opExtrude","SWEPT_FACE",FACE,{"disambiguationData":[OSD([sQuery(id+"F5.wireOp",EDGE,"E64")])]}),makeQuery(id+"F8.opExtrude","SWEPT_FACE",FACE,{"disambiguationData":[OSD([sQuery(id+"F7.wireOp",EDGE,"E141")])]})]});
            var Q36;
            Q36=makeQuery(id+"F9.opBoolean","INTERSECT",EDGE,{"derivedFrom":[makeQuery(id+"F6.opExtrude","SWEPT_FACE",FACE,{"disambiguationData":[OSD([sQuery(id+"F5.wireOp",EDGE,"E63")])]}),makeQuery(id+"F8.opExtrude","SWEPT_FACE",FACE,{"disambiguationData":[OSD([sQuery(id+"F7.wireOp",EDGE,"E141")])]})]});
            var Q37;
            Q37=makeQuery(id+"F9.opBoolean","INTERSECT",EDGE,{"derivedFrom":[makeQuery(id+"F6.opExtrude","SWEPT_FACE",FACE,{"disambiguationData":[OSD([sQuery(id+"F5.wireOp",EDGE,"E62")])]}),makeQuery(id+"F8.opExtrude","SWEPT_FACE",FACE,{"disambiguationData":[OSD([sQuery(id+"F7.wireOp",EDGE,"E141")])]})]});
            var Q38;
            Q38=makeQuery(id+"F9.opBoolean","INTERSECT",EDGE,{"derivedFrom":[makeQuery(id+"F6.opExtrude","SWEPT_FACE",FACE,{"disambiguationData":[OSD([sQuery(id+"F5.wireOp",EDGE,"E61")])]}),makeQuery(id+"F8.opExtrude","SWEPT_FACE",FACE,{"disambiguationData":[OSD([sQuery(id+"F7.wireOp",EDGE,"E141")])]})]});
            var Q39;
            Q39=makeQuery(id+"F9.opBoolean","INTERSECT",EDGE,{"derivedFrom":[makeQuery(id+"F6.opExtrude","SWEPT_FACE",FACE,{"disambiguationData":[OSD([sQuery(id+"F5.wireOp",EDGE,"E60")])]}),makeQuery(id+"F8.opExtrude","SWEPT_FACE",FACE,{"disambiguationData":[OSD([sQuery(id+"F7.wireOp",EDGE,"E141")])]})]});
            var Q40;
            Q40=makeQuery(id+"F9.opBoolean","INTERSECT",EDGE,{"derivedFrom":[makeQuery(id+"F6.opExtrude","SWEPT_FACE",FACE,{"disambiguationData":[OSD([sQuery(id+"F5.wireOp",EDGE,"E59")])]}),makeQuery(id+"F8.opExtrude","SWEPT_FACE",FACE,{"disambiguationData":[OSD([sQuery(id+"F7.wireOp",EDGE,"E141")])]})]});
            var Q41;
            Q41=makeQuery(id+"F9.opBoolean","INTERSECT",EDGE,{"derivedFrom":[makeQuery(id+"F6.opExtrude","SWEPT_FACE",FACE,{"disambiguationData":[OSD([sQuery(id+"F5.wireOp",EDGE,"E58")])]}),makeQuery(id+"F8.opExtrude","SWEPT_FACE",FACE,{"disambiguationData":[OSD([sQuery(id+"F7.wireOp",EDGE,"E141")])]})]});
            var Q42;
            Q42=makeQuery(id+"F9.opBoolean","INTERSECT",EDGE,{"derivedFrom":[makeQuery(id+"F6.opExtrude","SWEPT_FACE",FACE,{"disambiguationData":[OSD([sQuery(id+"F5.wireOp",EDGE,"E59")])]}),makeQuery(id+"F8.opExtrude","SWEPT_FACE",FACE,{"disambiguationData":[OSD([sQuery(id+"F7.wireOp",EDGE,"E141")])]})]});
            var Q43;
            Q43=makeQuery(id+"F9.opBoolean","INTERSECT",EDGE,{"derivedFrom":[makeQuery(id+"F6.opExtrude","SWEPT_FACE",FACE,{"disambiguationData":[OSD([sQuery(id+"F5.wireOp",EDGE,"E57")])]}),makeQuery(id+"F8.opExtrude","SWEPT_FACE",FACE,{"disambiguationData":[OSD([sQuery(id+"F7.wireOp",EDGE,"E141")])]})]});
            var Q44;
            Q44=makeQuery(id+"F9.opBoolean","INTERSECT",EDGE,{"derivedFrom":[makeQuery(id+"F6.opExtrude","SWEPT_FACE",FACE,{"disambiguationData":[OSD([sQuery(id+"F5.wireOp",EDGE,"E52")])]}),makeQuery(id+"F8.opExtrude","SWEPT_FACE",FACE,{"disambiguationData":[OSD([sQuery(id+"F7.wireOp",EDGE,"E141")])]})]});
            var Q45;
            Q45=makeQuery(id+"F9.opBoolean","INTERSECT",EDGE,{"derivedFrom":[makeQuery(id+"F6.opExtrude","SWEPT_FACE",FACE,{"disambiguationData":[OSD([sQuery(id+"F5.wireOp",EDGE,"E51")])]}),makeQuery(id+"F8.opExtrude","SWEPT_FACE",FACE,{"disambiguationData":[OSD([sQuery(id+"F7.wireOp",EDGE,"E141")])]})]});
            var Q46;
            Q46=makeQuery(id+"F9.opBoolean","INTERSECT",EDGE,{"derivedFrom":[makeQuery(id+"F6.opExtrude","SWEPT_FACE",FACE,{"disambiguationData":[OSD([sQuery(id+"F5.wireOp",EDGE,"E51")])]}),makeQuery(id+"F8.opExtrude","SWEPT_FACE",FACE,{"disambiguationData":[OSD([sQuery(id+"F7.wireOp",EDGE,"E141")])]})]});
            var Q47;
            Q47=makeQuery(id+"F9.opBoolean","INTERSECT",EDGE,{"derivedFrom":[makeQuery(id+"F6.opExtrude","SWEPT_FACE",FACE,{"disambiguationData":[OSD([sQuery(id+"F5.wireOp",EDGE,"E50")])]}),makeQuery(id+"F8.opExtrude","SWEPT_FACE",FACE,{"disambiguationData":[OSD([sQuery(id+"F7.wireOp",EDGE,"E141")])]})]});
            var Q48;
            Q48=makeQuery(id+"F9.opBoolean","INTERSECT",EDGE,{"derivedFrom":[makeQuery(id+"F6.opExtrude","SWEPT_FACE",FACE,{"disambiguationData":[OSD([sQuery(id+"F5.wireOp",EDGE,"E49")])]}),makeQuery(id+"F8.opExtrude","SWEPT_FACE",FACE,{"disambiguationData":[OSD([sQuery(id+"F7.wireOp",EDGE,"E141")])]})]});
            var Q49;
            Q49=makeQuery(id+"F9.opBoolean","INTERSECT",EDGE,{"derivedFrom":[makeQuery(id+"F6.opExtrude","SWEPT_FACE",FACE,{"disambiguationData":[OSD([sQuery(id+"F5.wireOp",EDGE,"E48")])]}),makeQuery(id+"F8.opExtrude","SWEPT_FACE",FACE,{"disambiguationData":[OSD([sQuery(id+"F7.wireOp",EDGE,"E141")])]})]});
            var Q50;
            Q50=makeQuery(id+"F9.opBoolean","INTERSECT",EDGE,{"derivedFrom":[makeQuery(id+"F6.opExtrude","SWEPT_FACE",FACE,{"disambiguationData":[OSD([sQuery(id+"F5.wireOp",EDGE,"E45")])]}),makeQuery(id+"F8.opExtrude","SWEPT_FACE",FACE,{"disambiguationData":[OSD([sQuery(id+"F7.wireOp",EDGE,"E141")])]})]});
            var Q51;
            Q51=makeQuery(id+"F9.opBoolean","INTERSECT",EDGE,{"derivedFrom":[makeQuery(id+"F6.opExtrude","SWEPT_FACE",FACE,{"disambiguationData":[OSD([sQuery(id+"F5.wireOp",EDGE,"E44")])]}),makeQuery(id+"F8.opExtrude","SWEPT_FACE",FACE,{"disambiguationData":[OSD([sQuery(id+"F7.wireOp",EDGE,"E141")])]})]});
            fillet(context, id + "F10", {"entities" : qUnion([Q0, Q1, Q2, Q3, Q4, Q5, Q6, Q7, Q8, Q9, Q10, Q11, Q12, Q13, Q14, Q15, Q16, Q17, Q18, Q19, Q20, Q21, Q22, Q23, Q24, Q25, Q26, Q27, Q28, Q29, Q30, Q31, Q32, Q33, Q34, Q35, Q36, Q37, Q38, Q39, Q40, Q41, Q42, Q43, Q44, Q45, Q46, Q47, Q48, Q49, Q50, Q51]), "radius" : 1 * mm, "tangentPropagation" : true, "allowEdgeOverflow" : false});
        }
        {
            var Q0;
            Q0=qCreatedBy(makeId("Right.planeOp"),FACE);
            cPlane(context, id + "F11", {"entities" : qUnion([Q0]), "cplaneType" : CPlaneType.OFFSET, "offset" : 165.7 * mm, "width" : 150 * mm, "height" : 150 * mm});
        }
        {
            var Q0;
            Q0=qCreatedBy(makeId("Right.planeOp"),FACE);
            cPlane(context, id + "F12", {"entities" : qUnion([Q0]), "cplaneType" : CPlaneType.OFFSET, "offset" : 690.8 * mm, "width" : 150 * mm, "height" : 150 * mm});
        }
        {
            var Q0;
            Q0=qCreatedBy(id+"F11.planeOp",FACE);
            var sketch = newSketch(context, id + "F13", { "sketchPlane" : qUnion([Q0])});
            skArc(sketch, "E142", {"start": v(-26.86, 0) * mm, "mid": v(0, -16) * mm, "end": v(26.86, 0) * mm});
            skLineSegment(sketch, "E143.0", {"start": v(-26.86, 0) * mm, "end": v(26.86, 0) * mm, "construction": true});
            skLineSegment(sketch, "E144", {"start": v(-26.86, 0) * mm, "end": v(26.86, 0) * mm});
            skSolve(sketch);
        }
        {
            var Q0;
            Q0=makeQuery(id+"F1.opExtrude","SWEPT_FACE",FACE,{"disambiguationData":[OSD([sQuery(id+"F0.wireOp",EDGE,"E13")])]});
            var sketch = newSketch(context, id + "F14", { "sketchPlane" : qUnion([Q0])});
            skLineSegment(sketch, "E145", {"start": v(-22, 7) * mm, "end": v(-22, 0) * mm});
            skLineSegment(sketch, "E146", {"start": v(-22, 0) * mm, "end": v(0, 0) * mm});
            skLineSegment(sketch, "E147", {"start": v(0, 0) * mm, "end": v(22, 0) * mm});
            skLineSegment(sketch, "E148", {"start": v(22, 0) * mm, "end": v(22, 7) * mm});
            skArc(sketch, "E149", {"start": v(22, 7) * mm, "mid": v(0, 7.6) * mm, "end": v(-22, 7) * mm});
            skSolve(sketch);
        }
        {
            var Q0;
            Q0 = qSketchRegion(id + "F14", true);
            extrude(context, id + "F15", {"entities" : qUnion([Q0]), "depth" : 5 * mm});
        }
        {
            var Q0;
            Q0=makeQuery(id+"F15.opExtrude","CAP_EDGE",EDGE,{"disambiguationData":[OSD([sQuery(id+"F14.wireOp",EDGE,"E149")])],"isStart":false});
            fillet(context, id + "F16", {"entities" : qUnion([Q0]), "radius" : 2.5 * mm, "tangentPropagation" : true, "allowEdgeOverflow" : false});
        }
        {
            var Q0;
            Q0=makeQuery(id+"F15.opExtrude","CAP_EDGE",EDGE,{"disambiguationData":[OSD([sQuery(id+"F14.wireOp",EDGE,"E146"),sQuery(id+"F14.wireOp",EDGE,"E147")])],"isStart":false});
            cPlane(context, id + "F17", {"entities" : qUnion([Q0]), "cplaneType" : CPlaneType.LINE_ANGLE, "offset" : 25 * mm, "angle" : 77 * degree, "width" : 150 * mm, "height" : 150 * mm});
        }
        {
            var Q0;
            Q0=qCreatedBy(id+"F17.planeOp",FACE);
            var sketch = newSketch(context, id + "F18", { "sketchPlane" : qUnion([Q0])});
            skLineSegment(sketch, "E150.0", {"start": v(-22, 155.4) * mm, "end": v(22, 155.4) * mm});
            skArc(sketch, "E151", {"start": v(-22, 155.4) * mm, "mid": v(0, 141.4) * mm, "end": v(22, 155.4) * mm});
            skSolve(sketch);
        }
        {
            var Q1;
            Q1 = qSketchRegion(id + "F13", true);
            var Q2;
            Q2 = qSketchRegion(id + "F18", true);
            loft(context, id + "F19", {"sheetProfilesArray" : [{ "sheetProfileEntities" : qUnion([Q1]) }, { "sheetProfileEntities" : qUnion([Q2]) }]});
        }
        {
            var Q0;
            Q0=qCreatedBy(id+"F17.planeOp",FACE);
            cPlane(context, id + "F20", {"entities" : qUnion([Q0]), "cplaneType" : CPlaneType.OFFSET, "offset" : 10 * mm, "width" : 150 * mm, "height" : 150 * mm});
        }
        {
            var Q0;
            Q0=qCreatedBy(id+"F17.planeOp",FACE);
            cPlane(context, id + "F21", {"entities" : qUnion([Q0]), "cplaneType" : CPlaneType.OFFSET, "offset" : 40 * mm, "width" : 150 * mm, "height" : 150 * mm});
        }
        {
            var Q0;
            Q0=qCreatedBy(id+"F21.planeOp",FACE);
            var sketch = newSketch(context, id + "F22", { "sketchPlane" : qUnion([Q0])});
            skLineSegment(sketch, "E152.0", {"start": v(22, 155.37) * mm, "end": v(-22, 155.37) * mm, "construction": true});
            skLineSegment(sketch, "E153", {"start": v(-72, 155.37) * mm, "end": v(78, 155.37) * mm});
            skLineSegment(sketch, "E154", {"start": v(78, 155.37) * mm, "end": v(78, 142.37) * mm});
            skLineSegment(sketch, "E155", {"start": v(78, 142.37) * mm, "end": v(-72, 142.37) * mm});
            skLineSegment(sketch, "E156", {"start": v(-72, 142.37) * mm, "end": v(-72, 155.37) * mm});
            skSolve(sketch);
        }
        {
            var Q0;
            Q0 = qSketchRegion(id + "F22", true);
            extrude(context, id + "F23", {"entities" : qUnion([Q0]), "depth" : 200 * mm});
        }
        {
            var Q0;
            Q0=qCreatedBy(id+"F20.planeOp",FACE);
            var sketch = newSketch(context, id + "F24", { "sketchPlane" : qUnion([Q0])});
            skLineSegment(sketch, "E157.0", {"start": v(22, 155.4) * mm, "end": v(-22, 155.4) * mm, "construction": true});
            skLineSegment(sketch, "E158", {"start": v(-26, 155.4) * mm, "end": v(26, 155.4) * mm});
            skArc(sketch, "E159", {"start": v(-26, 155.4) * mm, "mid": v(0, 141.4) * mm, "end": v(26, 155.4) * mm});
            skSolve(sketch);
        }
        {
            var Q1;
            Q1=makeQuery(id+"F19.opLoft","CAP_FACE",FACE,{"disambiguationData":[OSD([makeQuery(id+"F18.imprint","IMPRINT",FACE,{"disambiguationData":[TD([[makeQuery(id+"F18.imprint","IMPRINT",EDGE,{"derivedFrom":sQuery(id+"F18.wireOp",EDGE,"E151")}),1.0]])]})])],"isStart":true});
            var Q2;
            Q2=makeQuery(id+"F24.imprint","IMPRINT",FACE,{"disambiguationData":[TD([[makeQuery(id+"F24.imprint","IMPRINT",EDGE,{"derivedFrom":sQuery(id+"F24.wireOp",EDGE,"E158")}),-1.0]])]});
            loft(context, id + "F25", {"operationType" : NewBodyOperationType.ADD, "sheetProfilesArray" : [{ "sheetProfileEntities" : qUnion([Q1]) }, { "sheetProfileEntities" : qUnion([Q2]) }]});
        }
        {
            var Q1;
            Q1=makeQuery(id+"F25.opLoft","CAP_FACE",FACE,{"disambiguationData":[OSD([makeQuery(id+"F24.imprint","IMPRINT",FACE,{"disambiguationData":[TD([[makeQuery(id+"F24.imprint","IMPRINT",EDGE,{"derivedFrom":sQuery(id+"F24.wireOp",EDGE,"E158")}),-1.0]])]})])],"isStart":true});
            var Q2;
            Q2=makeQuery(id+"F23.opExtrude","CAP_FACE",FACE,{"disambiguationData":[OSD([sQuery(id+"F22.wireOp",EDGE,"E153"),sQuery(id+"F22.wireOp",EDGE,"E154"),sQuery(id+"F22.wireOp",EDGE,"E155"),sQuery(id+"F22.wireOp",EDGE,"E156")])],"isStart":true});
            loft(context, id + "F26", {"operationType" : NewBodyOperationType.ADD, "startCondition" : LoftEndDerivativeType.NORMAL_TO_PROFILE, "startMagnitude" : 1, "endCondition" : LoftEndDerivativeType.NORMAL_TO_PROFILE, "endMagnitude" : 1, "sheetProfilesArray" : [{ "sheetProfileEntities" : qUnion([Q1]) }, { "sheetProfileEntities" : qUnion([Q2]) }]});
        }
        {
            var Q0;
            Q0=makeQuery(id+"F23.opExtrude","SWEPT_FACE",FACE,{"disambiguationData":[OSD([sQuery(id+"F22.wireOp",EDGE,"E153")])]});
            var sketch = newSketch(context, id + "F27", { "sketchPlane" : qUnion([Q0])});
            skEllipticalArc(sketch, "E160.0", {"construction": true});
            skLineSegment(sketch, "E161", {"start": v(666.52, 19.2) * mm, "end": v(951.95, 19.2) * mm, "construction": true});
            skLineSegment(sketch, "E162", {"start": v(666.45, 10.77) * mm, "end": v(952.9, 10.77) * mm, "construction": true});
            skLineSegment(sketch, "E163", {"start": v(666.42, 2.75) * mm, "end": v(952.19, 2.75) * mm, "construction": true});
            skLineSegment(sketch, "E164", {"start": v(666.42, -4.96) * mm, "end": v(956.9, -4.96) * mm, "construction": true});
            skLineSegment(sketch, "E165", {"start": v(666.46, -12.47) * mm, "end": v(938.8, -12.47) * mm, "construction": true});
            skLineSegment(sketch, "E166", {"start": v(666.53, -19.87) * mm, "end": v(927.13, -19.87) * mm, "construction": true});
            skLineSegment(sketch, "E167", {"start": v(549.96, 0) * mm, "end": v(1014.75, 0) * mm, "construction": true});
            skPoint(sketch, "E167.startSnap0", {"position": v(666.42, 0) * mm});
            skCircle(sketch, "E168", {"center": v(726.53, -22.87) * mm, "radius": 3 * mm, "construction": true});
            skCircle(sketch, "E169", {"center": v(756.53, -15.47) * mm, "radius": 3 * mm, "construction": true});
            skCircle(sketch, "E170", {"center": v(786.53, -7.96) * mm, "radius": 3 * mm, "construction": true});
            skCircle(sketch, "E171", {"center": v(716.55, 22.2) * mm, "radius": 3 * mm, "construction": true});
            skCircle(sketch, "E172", {"center": v(776.55, 5.75) * mm, "radius": 3 * mm, "construction": true});
            skCircle(sketch, "E173", {"center": v(746.55, 13.77) * mm, "radius": 3 * mm, "construction": true});
            skFitSpline(sketch, "E174.0", {"points": [v(161.45, -26.86) * mm, v(331.97, -25.24) * mm, v(502.48, -23.62) * mm, v(673, -22) * mm], "construction": true});
            skFitSpline(sketch, "E175.0", {"points": [v(161.45, 26.86) * mm, v(331.97, 25.24) * mm, v(502.48, 23.62) * mm, v(673, 22) * mm], "construction": true});
            skLineSegment(sketch, "E176", {"start": v(673, 22) * mm, "end": v(673, -22) * mm});
            skLineSegment(sketch, "E177", {"start": v(715.2, -35.99) * mm, "end": v(829.6, -7.56) * mm, "construction": true});
            skLineSegment(sketch, "E178", {"start": v(677.63, 43.24) * mm, "end": v(811.9, 6.43) * mm, "construction": true});
            skLineSegment(sketch, "E179", {"start": v(673, -22) * mm, "end": v(673, 22) * mm});
            skArc(sketch, "E180", {"start": v(673, 22) * mm, "mid": v(692.11, 25.88) * mm, "end": v(708, 37.2) * mm});
            skArc(sketch, "E181", {"start": v(718, -37) * mm, "mid": v(696.75, -25.74) * mm, "end": v(673, -22) * mm});
            skArc(sketch, "E182", {"start": v(816.53, -15) * mm, "mid": v(766.56, -22.88) * mm, "end": v(718, -37) * mm});
            skArc(sketch, "E183", {"start": v(708, 37.2) * mm, "mid": v(754.01, 21.86) * mm, "end": v(801.55, 12.2) * mm});
            skArc(sketch, "E184", {"start": v(801.55, 12.2) * mm, "mid": v(805.25, -3.49) * mm, "end": v(816.53, -15) * mm});
            const initialGuessF27  = {"E160.0": [0.75783695409485, 0, 0, -1, 0.4064, 0.0914201084853467, 4.6582286475401675, 4.766549313229212]};
            skSetInitialGuess(sketch, initialGuessF27);
            skSolve(sketch);
        }
        {
            var Q0;
            Q0 = qSketchRegion(id + "F27", true);
            extrude(context, id + "F28", {"entities" : qUnion([Q0]), "operationType" : NewBodyOperationType.INTERSECT, "endBound" : BoundingType.THROUGH_ALL, "oppositeDirection" : true, "depth" : 25 * mm});
        }
    });
